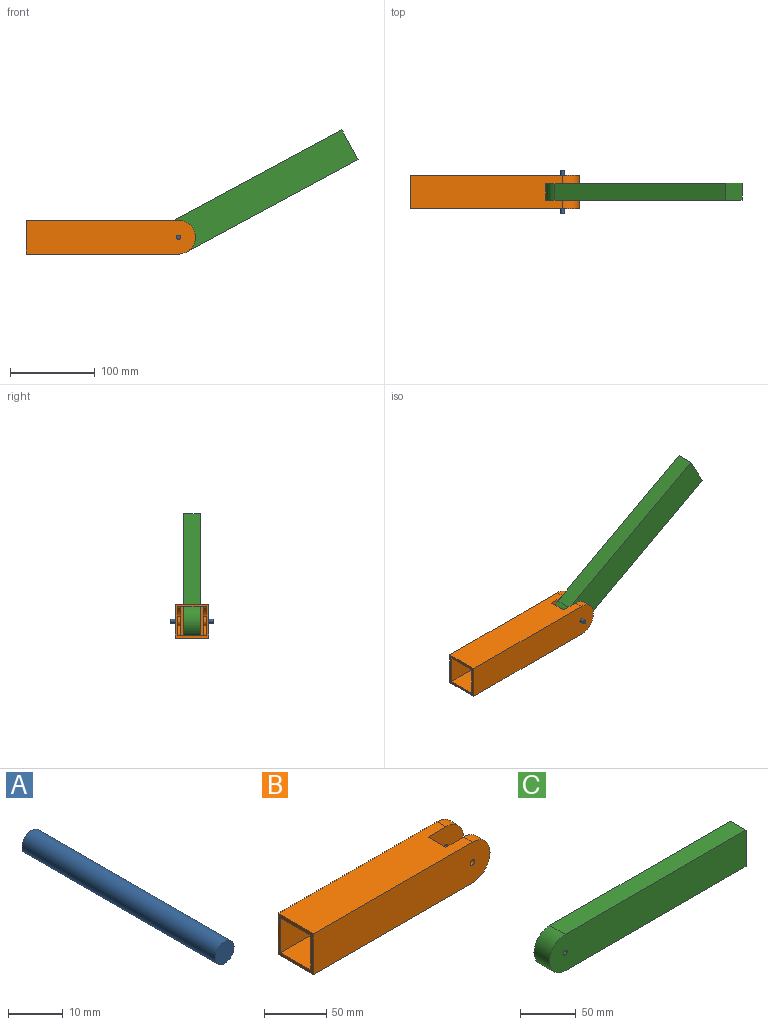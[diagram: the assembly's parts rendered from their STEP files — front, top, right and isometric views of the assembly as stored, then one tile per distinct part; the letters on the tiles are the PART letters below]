
ASSEMBLY  parts=3 mates=2
PART A: 3 faces, bbox 4.9x50x4.9 mm
  f0: cylinder r=2.45mm len=50mm, axis (0,1,0), area 769.7mm2, adj f1,f2
  f1: plane 4.9x4.9mm, normal (0,-1,0), area 18.9mm2, adj f0
  f2: plane 4.9x4.9mm, normal (0,1,0), area 18.9mm2, adj f0
PART B: 25 faces, bbox 200x40x40 mm
  f0: plane 40x40mm, normal (-1,0,0), area 444mm2, adj f2,f3,f4,f5,f14,f15,f16,f17
  f1: plane 20x3mm, normal (1,0,0), area 60mm2, adj f3,f6,f7,f15
  f2: plane 200x40mm, normal (0,1,0), area 7808.7mm2, adj f0,f3,f5,f10,f12
  f3: plane 180x40mm, normal (0,0,1), area 6800mm2, adj f0,f1,f2,f4,f6,f7,f11,f12
  f4: plane 200x40mm, normal (0,-1,0), area 7808.7mm2, adj f0,f3,f5,f9,f11
  f5: plane 180x40mm, normal (0,0,-1), area 6800mm2, adj f0,f2,f4,f6,f7,f8,f11,f12
  f6: plane 40x40mm, normal (0,-1,0), area 1408.7mm2, adj f1,f3,f5,f8,f10,f12,f20
  f7: plane 40x40mm, normal (0,1,0), area 1408.7mm2, adj f1,f3,f5,f8,f9,f11,f13
  f8: plane 20x3mm, normal (1,0,0), area 60mm2, adj f5,f6,f7,f17
  f9: cylinder r=2.5mm len=10mm, axis (0,-1,0), area 157.1mm2, adj f4,f7
  f10: cylinder r=2.5mm len=10mm, axis (0,-1,0), area 157.1mm2, adj f2,f6
  f11: cylinder r=20mm len=40mm, axis (0,-1,0), area 628.3mm2, adj f3,f4,f5,f7
  f12: cylinder r=20mm len=40mm, axis (0,-1,0), area 628.3mm2, adj f2,f3,f5,f6
  f13: plane 34x3mm, normal (-1,0,0), area 102mm2, adj f7,f15,f17,f19
  f14: plane 197x34mm, normal (0,-1,0), area 6478.9mm2, adj f0,f15,f17,f22,f24
  f15: plane 180x34mm, normal (0,0,-1), area 5600mm2, adj f0,f1,f13,f14,f16,f18,f19,f20
  f16: plane 197x34mm, normal (0,1,0), area 6478.9mm2, adj f0,f15,f17,f21,f23
  f17: plane 180x34mm, normal (0,0,1), area 5600mm2, adj f0,f8,f13,f14,f16,f18,f19,f20
  f18: plane 37x34mm, normal (0,1,0), area 1038.9mm2, adj f15,f17,f20,f22,f24
  f19: plane 37x34mm, normal (0,-1,0), area 1038.9mm2, adj f13,f15,f17,f21,f23
  f20: plane 34x3mm, normal (-1,0,0), area 102mm2, adj f6,f15,f17,f18
  f21: cylinder r=5.5mm len=11mm, axis (0,-1,0), area 138.2mm2, adj f16,f19
  f22: cylinder r=5.5mm len=11mm, axis (0,-1,0), area 138.2mm2, adj f14,f18
  f23: cylinder r=17mm len=34mm, axis (0,-1,0), area 213.6mm2, adj f15,f16,f17,f19
  f24: cylinder r=17mm len=34mm, axis (0,-1,0), area 213.6mm2, adj f14,f15,f17,f18
PART C: 7 faces, bbox 250x19.8x40 mm
  f0: plane 250x40mm, normal (0,-1,0), area 9809.5mm2, adj f1,f3,f4,f5,f6
  f1: plane 40x19.8mm, normal (1,0,0), area 792mm2, adj f0,f2,f3,f4
  f2: plane 250x40mm, normal (0,1,0), area 9809.5mm2, adj f1,f3,f4,f5,f6
  f3: plane 230x19.8mm, normal (0,0,-1), area 4554mm2, adj f0,f1,f2,f5
  f4: plane 230x19.8mm, normal (0,0,1), area 4554mm2, adj f0,f1,f2,f5
  f5: cylinder r=20mm len=40mm, axis (0,1,0), area 1244.1mm2, adj f0,f2,f3,f4
  f6: cylinder r=2.45mm len=19.8mm, axis (0,1,0), area 304.8mm2, adj f0,f2
PLACE A rot(axis=(0,-1,0),28.3deg) t=(-61.08,0,-68.3)mm
PLACE B t=(-82.57,0,17)mm
PLACE C rot(axis=(-0.97,0,-0.24),180deg) t=(-61.16,0.1,-68.35)mm
MATE fastened C.f5 <-> A.f0  axis (0,1,0) through (97.43,10,17)mm
MATE revolute A.f0 <-> B.f9  axis (0,1,0) through (97.43,25,17)mm
